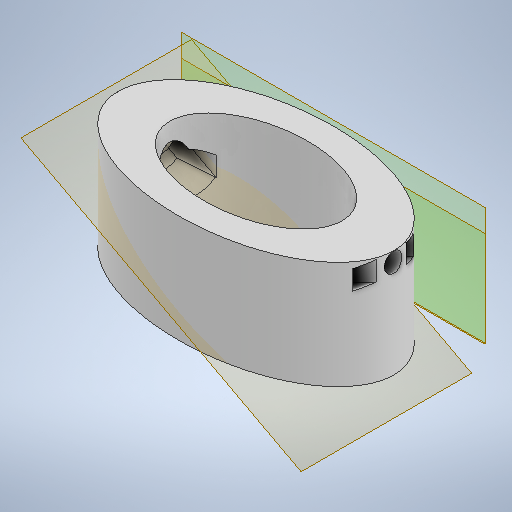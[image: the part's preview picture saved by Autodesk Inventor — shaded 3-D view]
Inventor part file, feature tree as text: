
AUTODESK INVENTOR PART (.ipt)
format: ipt  version: 2025.1 (Build 291241000, 241)  size: 354,304 bytes
history: native  units: mm
features: plane x5, sketch x5, extrude x4, projected_geometry x2, chamfer x1, mirror x1
ambient origin geometry x8: Origin, YZ Plane, XZ Plane, XY Plane, X Axis, Y Axis, Z Axis, Center Point
bodies: Volumenkörper1 (feature_tree)
feature tree (18):
  extrude  "Extrusion1"  Depth=20.0mm
  plane  "Arbeitsebene1"
  plane  "Arbeitsebene3"
  extrude  "Extrusion4"  Depth=12.0mm
  extrude  "Extrusion5"  Depth=4.886922mm
  extrude  "Extrusion6"  Depth=14.0mm
  sketch  "Skizze8"  dims[d14=4.0mm d15=5.0mm d16=10.0mm d17=0.0mm d18=0.0mm d19=0.0mm d20=4.0mm d21=10.0mm d22=0.0mm d23=3.0mm d24=2.0mm d25=6.632251mm]
  plane  "Arbeitsebene4"
  chamfer  "Fasen1"  Distance=5.0mm
  plane  "Arbeitsebene6"
  mirror  "Spiegeln2"
  sketch  "Skizze1"  dims[d0=32.0mm d1=20.0mm]
  plane  "Arbeitsebene2"
  sketch  "Skizze5"  dims[d2=25.0mm d3=0.0mm d4=12.0mm]
  sketch  "Skizze6"  dims[d5=18.0mm d10=4.886922mm d11=-18.5mm]
  projected_geometry  "Projizierte Kontur2"
  sketch  "Skizze7"  dims[d12=8.0mm d13=14.0mm]
  projected_geometry  "Projizierte Kontur3"
